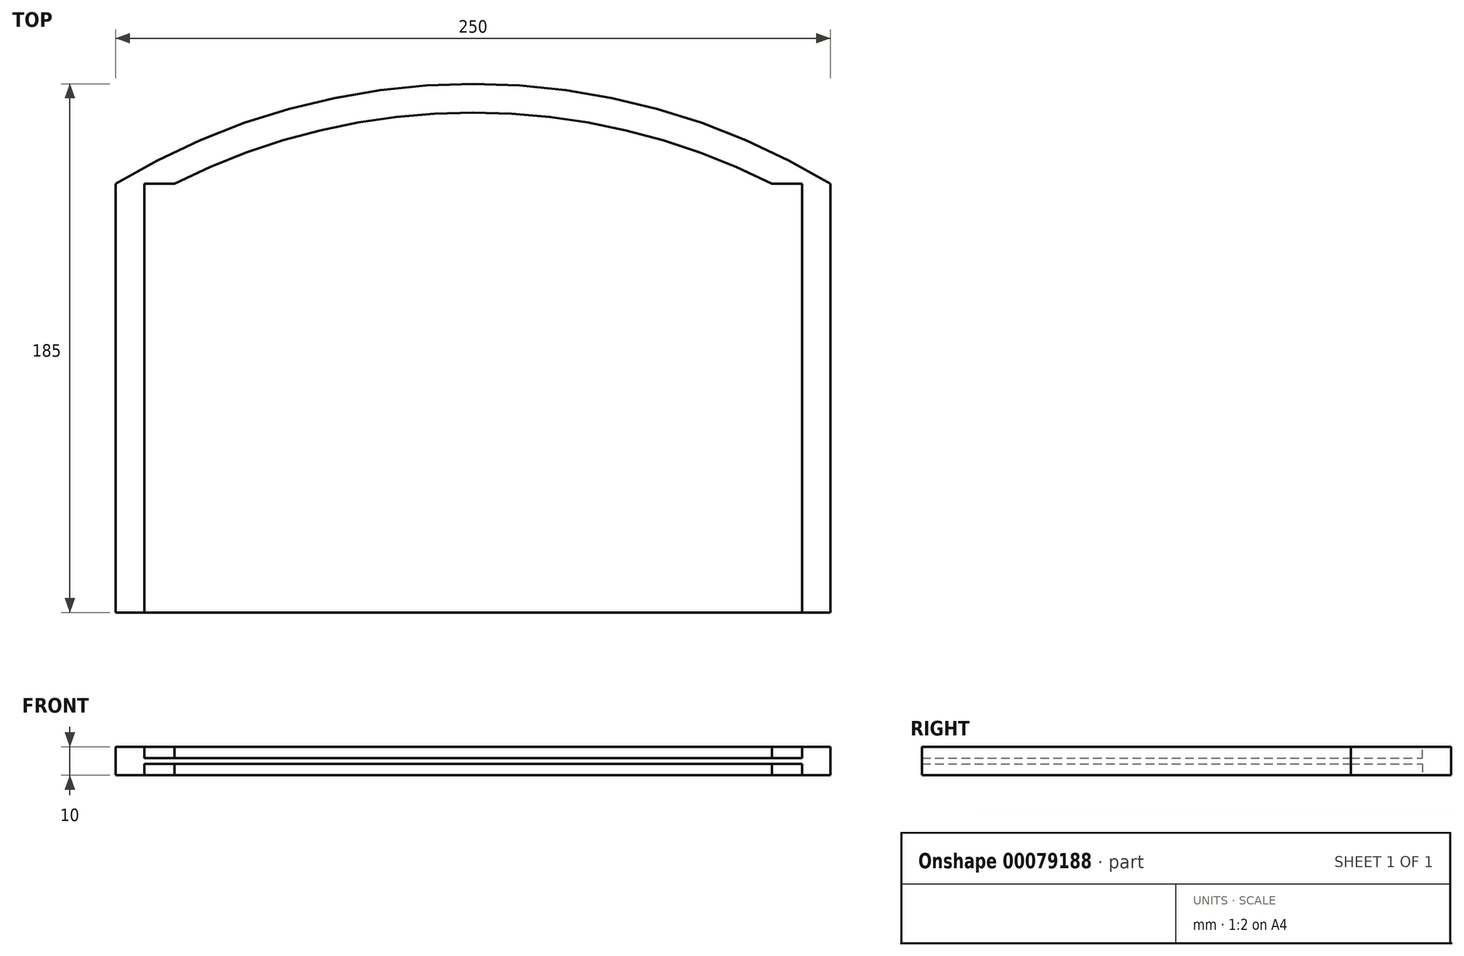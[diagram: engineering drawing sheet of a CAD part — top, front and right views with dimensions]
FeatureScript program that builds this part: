
annotation { "Feature Type Name" : "Feature", "Feature Type Description" : "" }
export const myFeature = defineFeature(function(context is Context, id is Id, definition is map)
    precondition{}
    {
        {
            var Q0;
            Q0=qCreatedBy(makeId("Top.planeOp"),FACE);
            var sketch = newSketch(context, id + "F0", { "sketchPlane" : qUnion([Q0])});
            skLineSegment(sketch, "E0.bottom", {"start": v(115, 0) * mm, "end": v(-115, 0) * mm});
            skLineSegment(sketch, "E0.top", {"start": v(115, 150) * mm, "end": v(104.45, 150) * mm});
            skLineSegment(sketch, "E0.left", {"start": v(115, 0) * mm, "end": v(115, 150) * mm});
            skLineSegment(sketch, "E0.right", {"start": v(-115, 0) * mm, "end": v(-115, 150) * mm});
            skLineSegment(sketch, "E1.0", {"start": v(125, 0) * mm, "end": v(125, 150) * mm});
            skLineSegment(sketch, "E2.0", {"start": v(-125, 0) * mm, "end": v(-125, 150) * mm});
            skPoint(sketch, "E3", {"position": v(0, 185) * mm});
            skArc(sketch, "E4", {"start": v(125, 150) * mm, "mid": v(0, 185) * mm, "end": v(-125, 150) * mm});
            skLineSegment(sketch, "E5", {"start": v(-125, 0) * mm, "end": v(125, 0) * mm});
            skArc(sketch, "E6.trimOffspring", {"start": v(104.45, 150) * mm, "mid": v(0, 175) * mm, "end": v(-104.45, 150) * mm});
            skLineSegment(sketch, "E7.trimOffspring", {"start": v(-104.45, 150) * mm, "end": v(-115, 150) * mm});
            skSolve(sketch);
        }
        {
            var Q0;
            Q0=makeQuery(id+"F0.imprint","IMPRINT",FACE,{"disambiguationData":[TD([[makeQuery(id+"F0.imprint","IMPRINT",EDGE,{"derivedFrom":sQuery(id+"F0.wireOp",EDGE,"E0.top")}),-1.0]])]});
            var Q1;
            Q1=makeQuery(id+"F0.imprint","IMPRINT",FACE,{"disambiguationData":[TD([[makeQuery(id+"F0.imprint","IMPRINT",EDGE,{"derivedFrom":sQuery(id+"F0.wireOp",EDGE,"E0.top")}),1.0]])]});
            extrude(context, id + "F1", {"entities" : qUnion([Q0, Q1]), "depth" : 10 * mm, "offsetDistance" : 25 * mm});
        }
        {
            var Q0;
            Q0=makeQuery(id+"F1.opExtrude","CAP_FACE",FACE,{"disambiguationData":[OSD([sQuery(id+"F0.wireOp",EDGE,"E1.0"),sQuery(id+"F0.wireOp",EDGE,"E2.0"),sQuery(id+"F0.wireOp",EDGE,"E4"),sQuery(id+"F0.wireOp",EDGE,"E5")])],"isStart":false});
            var sketch = newSketch(context, id + "F2", { "sketchPlane" : qUnion([Q0])});
            skLineSegment(sketch, "E8.0", {"start": v(-115, 0) * mm, "end": v(-115, 150) * mm});
            skLineSegment(sketch, "E9.0", {"start": v(115, 150) * mm, "end": v(104.45, 150) * mm});
            skLineSegment(sketch, "E10.0", {"start": v(115, 0) * mm, "end": v(115, 150) * mm});
            skArc(sketch, "E11.0", {"start": v(104.45, 150) * mm, "mid": v(0, 175) * mm, "end": v(-104.45, 150) * mm});
            skLineSegment(sketch, "E12.0", {"start": v(-104.45, 150) * mm, "end": v(-115, 150) * mm});
            skSolve(sketch);
        }
        {
            var Q0;
            {var subQ0=sQuery(id+"F2.wireOp",EDGE,"E8.0");Q0=makeQuery(id+"F2.imprint","IMPRINT",FACE,{"disambiguationData":[TD([[makeQuery(id+"F2.imprint","IMPRINT",EDGE,{"derivedFrom":subQ0}),-1.0]])]});}
            extrude(context, id + "F3", {"entities" : qUnion([Q0]), "operationType" : NewBodyOperationType.REMOVE, "oppositeDirection" : true, "depth" : 4 * mm, "offsetDistance" : 25 * mm});
        }
        {
            var Q0;
            Q0=makeQuery(id+"F0.imprint","IMPRINT",FACE,{"disambiguationData":[TD([[makeQuery(id+"F0.imprint","IMPRINT",EDGE,{"derivedFrom":sQuery(id+"F0.wireOp",EDGE,"E0.top")}),1.0]])]});
            extrude(context, id + "F4", {"entities" : qUnion([Q0]), "operationType" : NewBodyOperationType.REMOVE, "depth" : 4 * mm, "offsetDistance" : 25 * mm});
        }
    });
